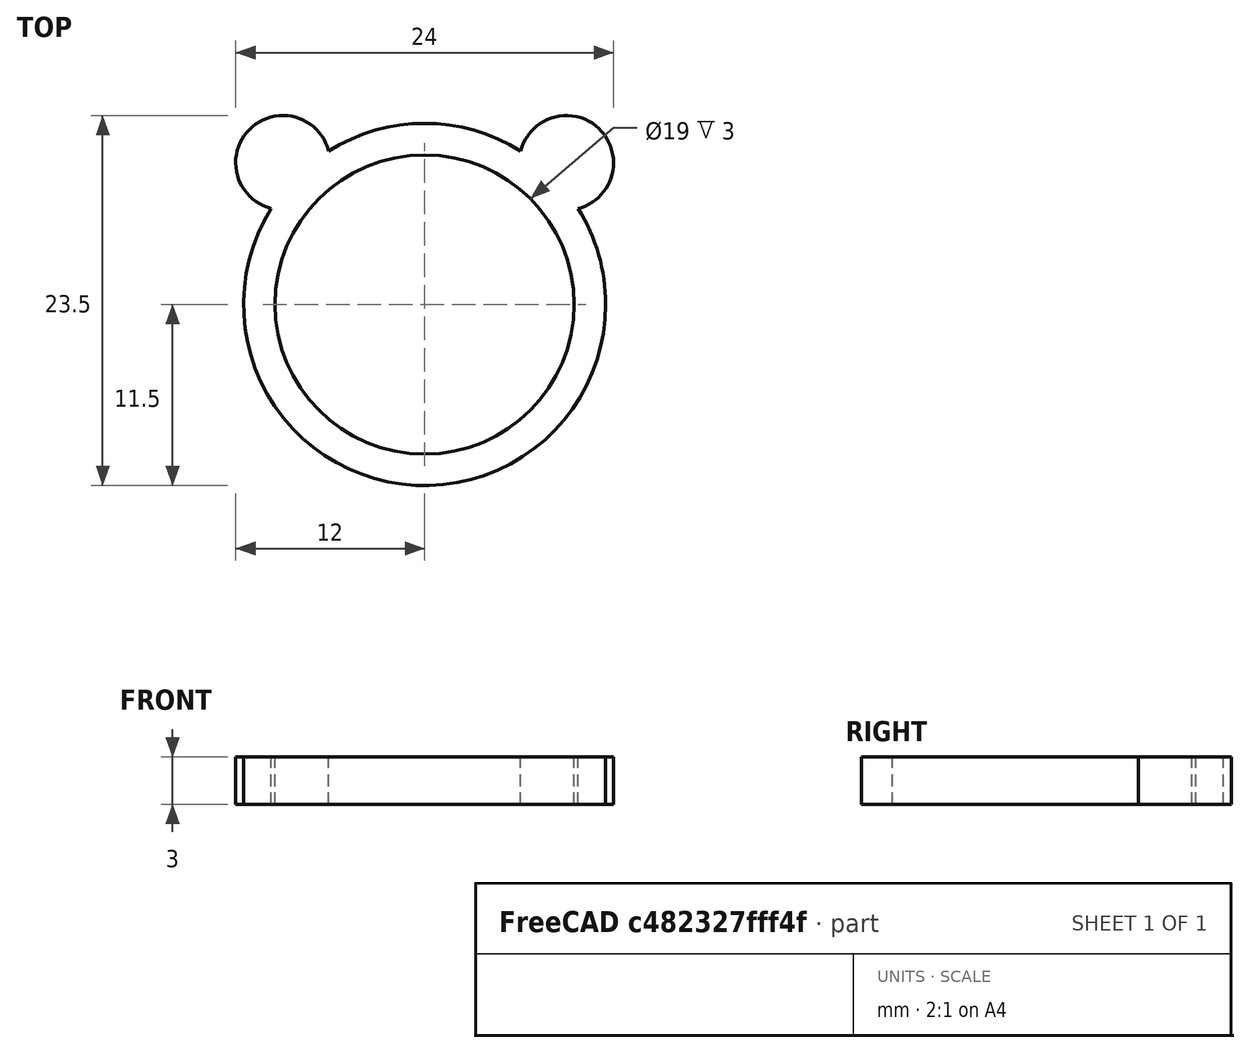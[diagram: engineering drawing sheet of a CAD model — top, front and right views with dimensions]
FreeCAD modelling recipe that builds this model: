
FCSTD DOCUMENT  (FreeCAD 0.16R6707 (Git))
Label: 07-anillo-osito
License: All rights reserved
LicenseURL: http://en.wikipedia.org/wiki/All_rights_reserved
objects: Part::Cylinder×4, Part::Cut×1, Part::MultiFuse×1
note: 6 computed .brp shape members not serialized (recipe doc carries the construction recipe); baked Part::Feature solids carry a one-line shape summary decoded from their .brp

FEATURE [Part::Cylinder] Cylinder  label="Cilindro-exterior"
  Angle = 360
  Height = 3
  Radius = 11.5
  expr: Radius = 23 / 2
FEATURE [Part::Cylinder] Cylinder001  label="Cilindro-interior"
  Angle = 360
  Height = 10
  Placement = pos=(0,0,-4) rot=(0,0,1;0rad)
  Radius = 9.5
  expr: Radius = 19 / 2
FEATURE [Part::Cut] Cut  label="cuerpo-anillo"
  Base = -> Cylinder
  Tool = -> Cylinder001
FEATURE [Part::Cylinder] Cylinder002  label="Oreja-izda"
  Angle = 360
  Height = 3
  Placement = pos=(-9,9,0) rot=(0,0,1;0rad)
  Radius = 3
FEATURE [Part::Cylinder] Cylinder003  label="Oreja-decha"
  Angle = 360
  Height = 3
  Placement = pos=(9,9,0) rot=(0,0,1;0rad)
  Radius = 3
FEATURE [Part::MultiFuse] Fusion  label="Anillo-final"
  Shapes = -> [Cylinder002,Cylinder003,Cut]
